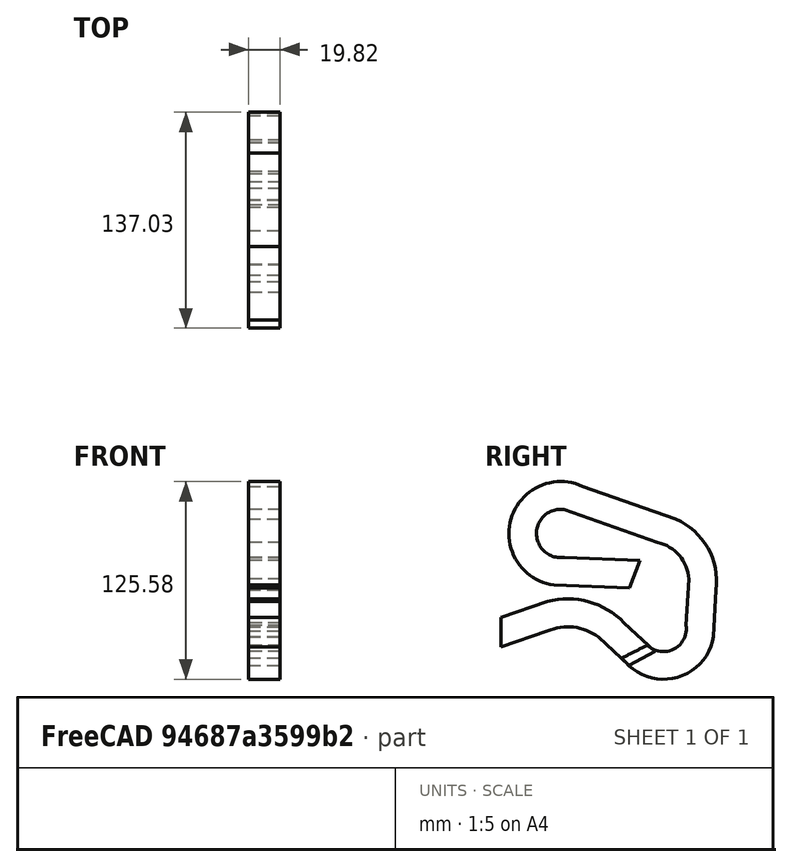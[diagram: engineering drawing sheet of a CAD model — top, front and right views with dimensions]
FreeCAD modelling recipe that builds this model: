
FCSTD DOCUMENT  (FreeCAD 1.0R38806 (Git))
Label: tubo seccion
License: All rights reserved
LicenseURL: http://en.wikipedia.org/wiki/All_rights_reserved
objects: Sketcher::SketchObject×2, PartDesign::Body×1, Part::Sweep×1
note: 6 computed .brp shape members not serialized (recipe doc carries the construction recipe); baked Part::Feature solids carry a one-line shape summary decoded from their .brp

FEATURE [Sketcher::SketchObject] Sketch
  ArcFitTolerance = 1e-06
  AttachmentSupport = -> [XZ_Plane]
  FullyConstrained = false
  MakeInternals = false
  MapMode = 5
  Placement = pos=(0,0,0) rot=(1,0,0;1.5708rad)
  sketch-geometry (4):
    g0: LineSegment StartX=-9.91425 StartY=9.3714 StartZ=0 EndX=-9.91425 EndY=-9.3714 EndZ=0
    g1: LineSegment StartX=-9.91425 StartY=-9.3714 StartZ=0 EndX=9.91425 EndY=-9.3714 EndZ=0
    g2: LineSegment StartX=9.91425 StartY=-9.3714 StartZ=0 EndX=9.91425 EndY=9.3714 EndZ=0
    g3: LineSegment StartX=9.91425 StartY=9.3714 StartZ=0 EndX=-9.91425 EndY=9.3714 EndZ=0
  constraints (8):
    c: Coincident(g0,g1)
    c: Coincident(g1,g2)
    c: Coincident(g2,g3)
    c: Coincident(g3,g0)
    c: Vertical(g2)
    c: Horizontal(g1)
    c: Symmetric(g2,g0,g-2)
    c: Symmetric(g0,g0,g-1)
FEATURE [Sketcher::SketchObject] Sketch001
  ArcFitTolerance = 1e-06
  AttachmentSupport = -> [YZ_Plane]
  FullyConstrained = false
  MakeInternals = false
  MapMode = 5
  Placement = pos=(0,0,0) rot=(0.57735,0.57735,0.57735;2.0944rad)
  sketch-geometry (9):
    g0: LineSegment StartX=0 StartY=0 StartZ=0 EndX=29.6195 EndY=9.97292 EndZ=0
    g1: LineSegment StartX=70.0346 StartY=1.35808 StartZ=0 EndX=87.2811 EndY=-14.5423 EndZ=0
    g2: LineSegment StartX=126.307 StartY=0.828808 StartZ=0 EndX=127.99 EndY=30.2005 EndZ=0
    g3: LineSegment StartX=105.233 StartY=64.3687 StartZ=0 EndX=45.9573 EndY=85.2312 EndZ=0
    g4: LineSegment StartX=37.0472 StartY=38.6755 StartZ=0 EndX=85.1128 EndY=36.7624 EndZ=0
    g5: ArcOfCircle CenterX=42.5556 CenterY=-28.4472 CenterZ=0 NormalX=0 NormalY=0 NormalZ=1 AngleXU=0 Radius=40.5395 StartAngle=0.825986 EndAngle=1.89557
    g6: ArcOfCircle CenterX=103.246 CenterY=2.15042 CenterZ=0 NormalX=0 NormalY=0 NormalZ=1 AngleXU=0 Radius=23.0984 StartAngle=3.94926 EndAngle=6.22594
    g7: ArcOfCircle CenterX=93.8949 CenterY=32.1545 CenterZ=0 NormalX=0 NormalY=0 NormalZ=1 AngleXU=0 Radius=34.1513 StartAngle=6.22594 EndAngle=7.51557
    g8: ArcOfCircle CenterX=38.0004 CenterY=62.6235 CenterZ=0 NormalX=0 NormalY=0 NormalZ=1 AngleXU=0 Radius=23.967 StartAngle=1.23238 EndAngle=4.67261
  constraints (9):
    c: Coincident(g0,g-1)
    c: Tangent(g0,g5) = 1.5708
    c: Tangent(g1,g5) = 1.5708
    c: Tangent(g2,g6) = -1.5708
    c: Tangent(g2,g7) = -1.5708
    c: Tangent(g3,g7) = -1.5708
    c: Tangent(g3,g8) = -1.5708
    c: Tangent(g4,g8) = -1.5708
    c: Coincident(g1,g6)
FEATURE [PartDesign::Body] Body
  AllowCompound = false
  Group = -> [Sketch,Sketch001]
  Origin = -> Origin
FEATURE [Part::Sweep] Sweep
  Frenet = true
  Sections = -> [Sketch]
  Solid = true
  Spine = -> Sketch001
  Transition = 1
